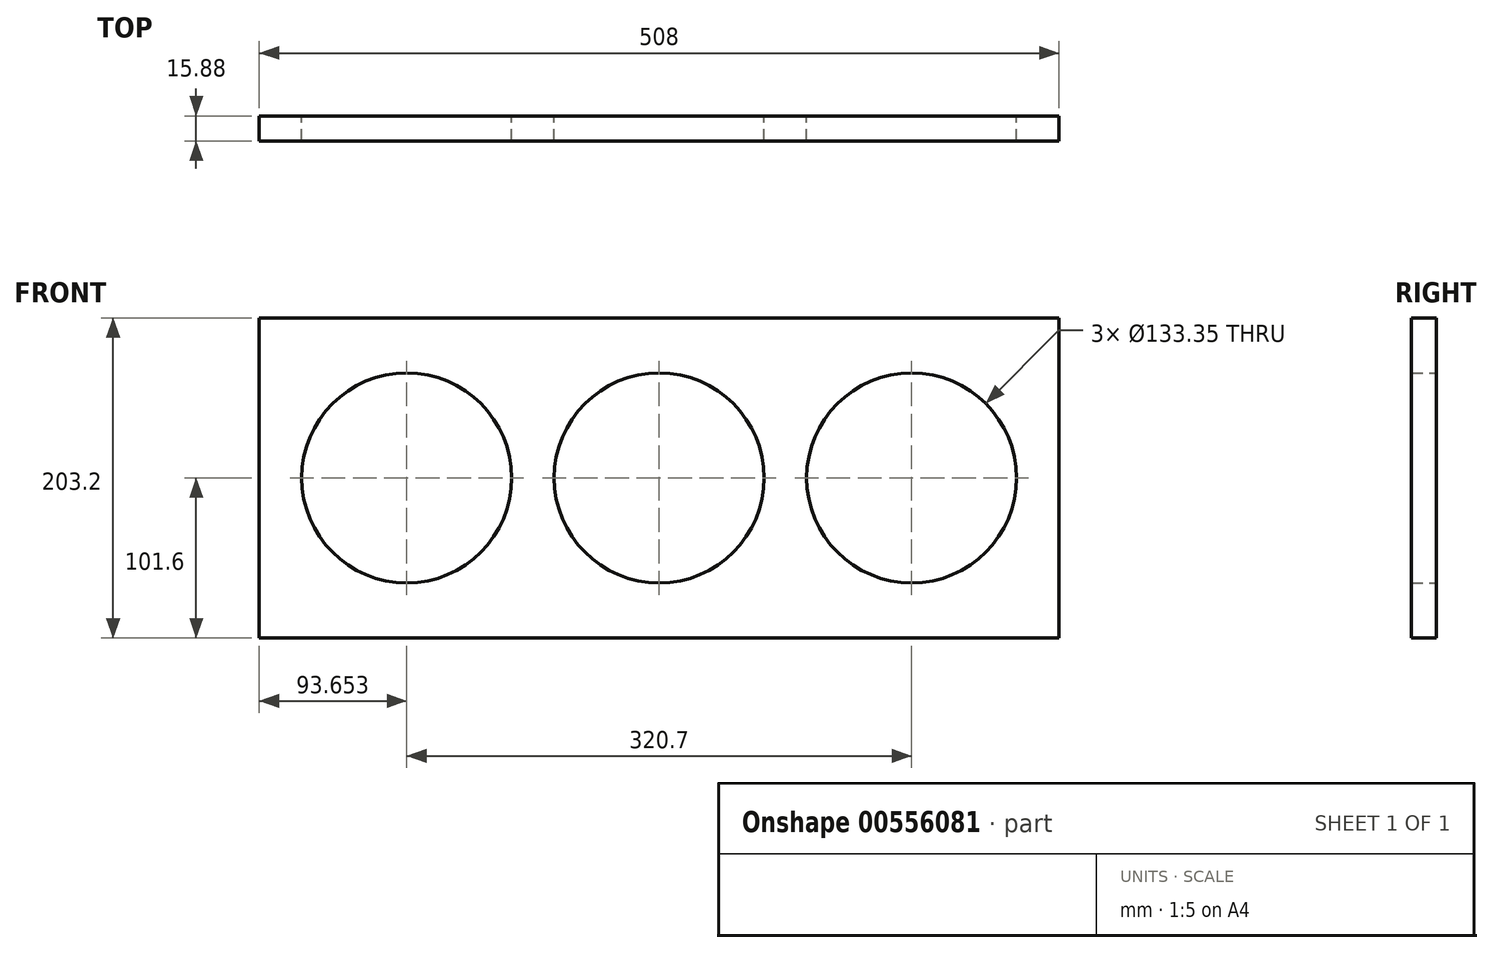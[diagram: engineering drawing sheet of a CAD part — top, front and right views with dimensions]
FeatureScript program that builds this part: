
annotation { "Feature Type Name" : "Feature", "Feature Type Description" : "" }
export const myFeature = defineFeature(function(context is Context, id is Id, definition is map)
    precondition{}
    {
        {
            var Q0;
            Q0=qCreatedBy(makeId("Front.planeOp"),FACE);
            var sketch = newSketch(context, id + "F0", { "sketchPlane" : qUnion([Q0])});
            skLineSegment(sketch, "E0", {"start": v(-74.88, 43.98) * mm, "end": v(433.12, 43.98) * mm});
            skLineSegment(sketch, "E1", {"start": v(433.12, 43.98) * mm, "end": v(433.12, -159.22) * mm});
            skLineSegment(sketch, "E2", {"start": v(433.12, -159.22) * mm, "end": v(-74.88, -159.22) * mm});
            skLineSegment(sketch, "E3", {"start": v(-74.88, -159.22) * mm, "end": v(-74.88, 43.98) * mm});
            skCircle(sketch, "E4", {"center": v(179.12, -57.62) * mm, "radius": 66.68 * mm});
            skPoint(sketch, "E5.end.orphan", {"position": v(179.12, 43.98) * mm});
            skCircle(sketch, "E6", {"center": v(18.77, -57.62) * mm, "radius": 66.68 * mm});
            skCircle(sketch, "E7", {"center": v(339.47, -57.62) * mm, "radius": 66.68 * mm});
            skPoint(sketch, "E8.orphan", {"position": v(18.77, 43.98) * mm});
            skSolve(sketch);
        }
        {
            var Q0;
            Q0=makeQuery(id+"F0.imprint","IMPRINT",FACE,{"disambiguationData":[TD([[makeQuery(id+"F0.imprint","IMPRINT",EDGE,{"derivedFrom":sQuery(id+"F0.wireOp",EDGE,"E0")}),-1.0]])]});
            extrude(context, id + "F1", {"entities" : qUnion([Q0]), "depth" : 15.88 * mm, "offsetDistance" : 25.4 * mm});
        }
    });
